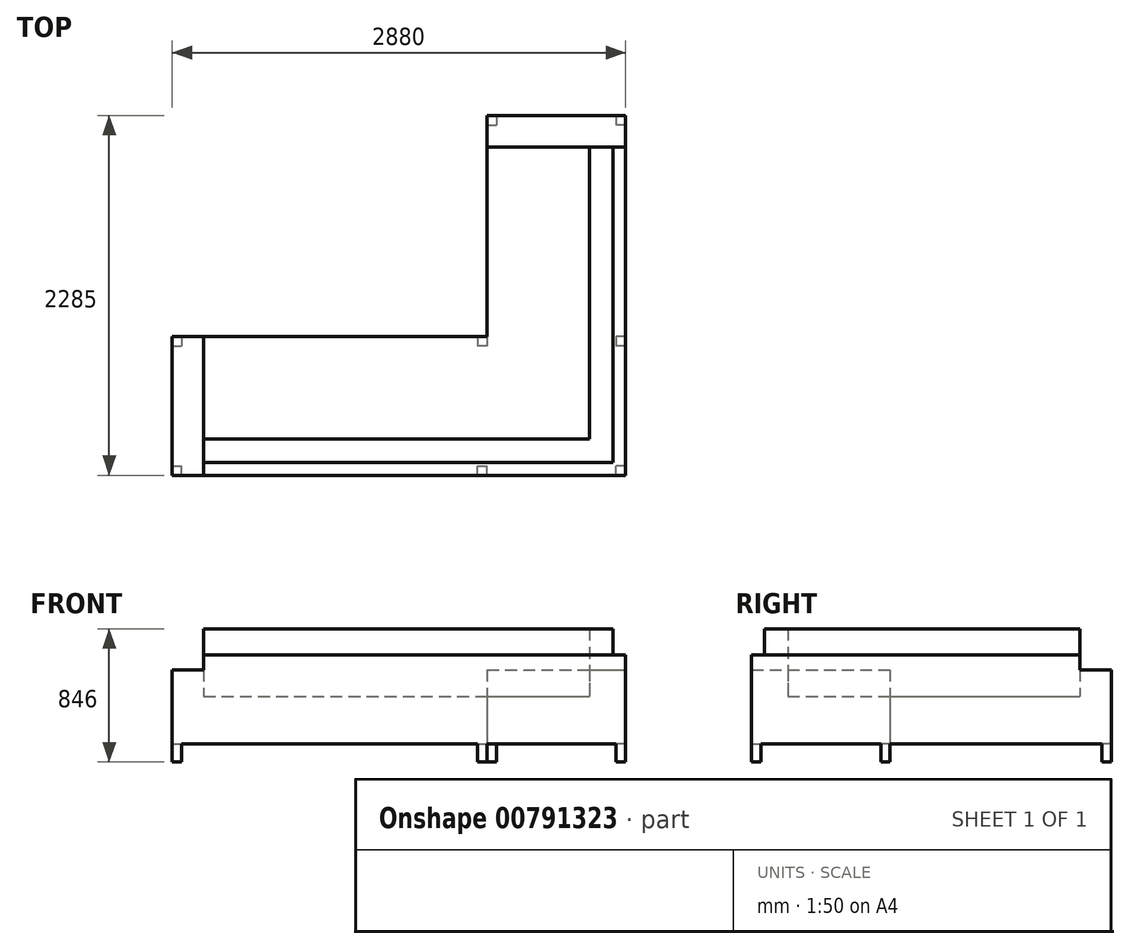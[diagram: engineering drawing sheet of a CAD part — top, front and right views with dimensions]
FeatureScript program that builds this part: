
annotation { "Feature Type Name" : "Feature", "Feature Type Description" : "" }
export const myFeature = defineFeature(function(context is Context, id is Id, definition is map)
    precondition{}
    {
        {
            var Q0;
            Q0=qCreatedBy(makeId("Top.planeOp"),FACE);
            var sketch = newSketch(context, id + "F0", { "sketchPlane" : qUnion([Q0])});
            skLineSegment(sketch, "E0", {"start": v(0, 0) * mm, "end": v(0, 1405) * mm});
            skLineSegment(sketch, "E1", {"start": v(0, 1405) * mm, "end": v(880, 1405) * mm});
            skLineSegment(sketch, "E2", {"start": v(880, 1405) * mm, "end": v(880, -880) * mm});
            skLineSegment(sketch, "E3", {"start": v(880, -880) * mm, "end": v(-2000, -880) * mm});
            skLineSegment(sketch, "E4", {"start": v(-2000, -880) * mm, "end": v(-2000, 0) * mm});
            skLineSegment(sketch, "E5", {"start": v(-2000, 0) * mm, "end": v(0, 0) * mm});
            skSolve(sketch);
        }
        {
            var Q0;
            Q0=makeQuery(id+"F0.imprint","IMPRINT",FACE,{"disambiguationData":[TD([[makeQuery(id+"F0.imprint","IMPRINT",EDGE,{"derivedFrom":sQuery(id+"F0.wireOp",EDGE,"E0")}),-1.0]])]});
            extrude(context, id + "F1", {"entities" : qUnion([Q0]), "depth" : 300 * mm, "offsetDistance" : 25 * mm});
        }
        {
            var Q0;
            Q0=makeQuery(id+"F1.opExtrude","CAP_FACE",FACE,{"disambiguationData":[OSD([sQuery(id+"F0.wireOp",EDGE,"E0"),sQuery(id+"F0.wireOp",EDGE,"E1"),sQuery(id+"F0.wireOp",EDGE,"E2"),sQuery(id+"F0.wireOp",EDGE,"E3"),sQuery(id+"F0.wireOp",EDGE,"E4"),sQuery(id+"F0.wireOp",EDGE,"E5")])],"isStart":true});
            var sketch = newSketch(context, id + "F2", { "sketchPlane" : qUnion([Q0])});
            skLineSegment(sketch, "E6.bottom", {"start": v(0, -1405) * mm, "end": v(60, -1405) * mm});
            skLineSegment(sketch, "E6.top", {"start": v(0, -1345) * mm, "end": v(60, -1345) * mm});
            skLineSegment(sketch, "E6.left", {"start": v(0, -1405) * mm, "end": v(0, -1345) * mm});
            skLineSegment(sketch, "E6.right", {"start": v(60, -1405) * mm, "end": v(60, -1345) * mm});
            skLineSegment(sketch, "E7.bottom", {"start": v(880, -1405) * mm, "end": v(820, -1405) * mm});
            skLineSegment(sketch, "E7.top", {"start": v(880, -1345) * mm, "end": v(820, -1345) * mm});
            skLineSegment(sketch, "E7.left", {"start": v(880, -1405) * mm, "end": v(880, -1345) * mm});
            skLineSegment(sketch, "E7.right", {"start": v(820, -1405) * mm, "end": v(820, -1345) * mm});
            skLineSegment(sketch, "E8.bottom", {"start": v(-2000, 0) * mm, "end": v(-1940, 0) * mm});
            skLineSegment(sketch, "E8.top", {"start": v(-2000, 60) * mm, "end": v(-1940, 60) * mm});
            skLineSegment(sketch, "E8.left", {"start": v(-2000, 0) * mm, "end": v(-2000, 60) * mm});
            skLineSegment(sketch, "E8.right", {"start": v(-1940, 0) * mm, "end": v(-1940, 60) * mm});
            skLineSegment(sketch, "E9.bottom", {"start": v(-2000, 880) * mm, "end": v(-1940, 880) * mm});
            skLineSegment(sketch, "E9.top", {"start": v(-2000, 820) * mm, "end": v(-1940, 820) * mm});
            skLineSegment(sketch, "E9.left", {"start": v(-2000, 880) * mm, "end": v(-2000, 820) * mm});
            skLineSegment(sketch, "E9.right", {"start": v(-1940, 880) * mm, "end": v(-1940, 820) * mm});
            skLineSegment(sketch, "E10.bottom", {"start": v(0, 0) * mm, "end": v(-60, 0) * mm});
            skLineSegment(sketch, "E10.top", {"start": v(0, 60) * mm, "end": v(-60, 60) * mm});
            skLineSegment(sketch, "E10.left", {"start": v(0, 0) * mm, "end": v(0, 60) * mm});
            skLineSegment(sketch, "E10.right", {"start": v(-60, 0) * mm, "end": v(-60, 60) * mm});
            skLineSegment(sketch, "E11.bottom", {"start": v(-60, 880) * mm, "end": v(0, 880) * mm});
            skLineSegment(sketch, "E11.top", {"start": v(-60, 820) * mm, "end": v(0, 820) * mm});
            skLineSegment(sketch, "E11.left", {"start": v(-60, 880) * mm, "end": v(-60, 820) * mm});
            skLineSegment(sketch, "E11.right", {"start": v(0, 880) * mm, "end": v(0, 820) * mm});
            skLineSegment(sketch, "E12.bottom", {"start": v(880, 880) * mm, "end": v(820, 880) * mm});
            skLineSegment(sketch, "E12.top", {"start": v(880, 820) * mm, "end": v(820, 820) * mm});
            skLineSegment(sketch, "E12.left", {"start": v(880, 880) * mm, "end": v(880, 820) * mm});
            skLineSegment(sketch, "E12.right", {"start": v(820, 880) * mm, "end": v(820, 820) * mm});
            skLineSegment(sketch, "E13.bottom", {"start": v(880, 0) * mm, "end": v(820, 0) * mm});
            skLineSegment(sketch, "E13.top", {"start": v(880, 60) * mm, "end": v(820, 60) * mm});
            skLineSegment(sketch, "E13.left", {"start": v(880, 0) * mm, "end": v(880, 60) * mm});
            skLineSegment(sketch, "E13.right", {"start": v(820, 0) * mm, "end": v(820, 60) * mm});
            skSolve(sketch);
        }
        {
            var Q0;
            Q0=makeQuery(id+"F2.imprint","IMPRINT",FACE,{"disambiguationData":[TD([[makeQuery(id+"F2.imprint","IMPRINT",EDGE,{"derivedFrom":sQuery(id+"F2.wireOp",EDGE,"E9.bottom")}),1.0]])]});
            var Q1;
            Q1=makeQuery(id+"F2.imprint","IMPRINT",FACE,{"disambiguationData":[TD([[makeQuery(id+"F2.imprint","IMPRINT",EDGE,{"derivedFrom":sQuery(id+"F2.wireOp",EDGE,"E8.bottom")}),1.0]])]});
            var Q2;
            Q2=makeQuery(id+"F2.imprint","IMPRINT",FACE,{"disambiguationData":[TD([[makeQuery(id+"F2.imprint","IMPRINT",EDGE,{"derivedFrom":sQuery(id+"F2.wireOp",EDGE,"E10.bottom")}),1.0]])]});
            var Q3;
            Q3=makeQuery(id+"F2.imprint","IMPRINT",FACE,{"disambiguationData":[TD([[makeQuery(id+"F2.imprint","IMPRINT",EDGE,{"derivedFrom":sQuery(id+"F2.wireOp",EDGE,"E11.bottom")}),1.0]])]});
            var Q4;
            Q4=makeQuery(id+"F2.imprint","IMPRINT",FACE,{"disambiguationData":[TD([[makeQuery(id+"F2.imprint","IMPRINT",EDGE,{"derivedFrom":sQuery(id+"F2.wireOp",EDGE,"E12.bottom")}),1.0]])]});
            var Q5;
            Q5=makeQuery(id+"F2.imprint","IMPRINT",FACE,{"disambiguationData":[TD([[makeQuery(id+"F2.imprint","IMPRINT",EDGE,{"derivedFrom":sQuery(id+"F2.wireOp",EDGE,"E13.bottom")}),-1.0]])]});
            var Q6;
            Q6=makeQuery(id+"F2.imprint","IMPRINT",FACE,{"disambiguationData":[TD([[makeQuery(id+"F2.imprint","IMPRINT",EDGE,{"derivedFrom":sQuery(id+"F2.wireOp",EDGE,"E6.bottom")}),1.0]])]});
            var Q7;
            Q7=makeQuery(id+"F2.imprint","IMPRINT",FACE,{"disambiguationData":[TD([[makeQuery(id+"F2.imprint","IMPRINT",EDGE,{"derivedFrom":sQuery(id+"F2.wireOp",EDGE,"E7.bottom")}),1.0]])]});
            extrude(context, id + "F3", {"entities" : qUnion([Q0, Q1, Q2, Q3, Q4, Q5, Q6, Q7]), "operationType" : NewBodyOperationType.ADD, "depth" : 116 * mm, "offsetDistance" : 25 * mm});
        }
        {
            var Q0;
            Q0=makeQuery(id+"F1.opExtrude","CAP_FACE",FACE,{"disambiguationData":[OSD([sQuery(id+"F0.wireOp",EDGE,"E0"),sQuery(id+"F0.wireOp",EDGE,"E1"),sQuery(id+"F0.wireOp",EDGE,"E2"),sQuery(id+"F0.wireOp",EDGE,"E3"),sQuery(id+"F0.wireOp",EDGE,"E4"),sQuery(id+"F0.wireOp",EDGE,"E5")])],"isStart":false});
            var sketch = newSketch(context, id + "F4", { "sketchPlane" : qUnion([Q0])});
            skLineSegment(sketch, "E14.bottom", {"start": v(0, 1405) * mm, "end": v(880, 1405) * mm});
            skLineSegment(sketch, "E14.top", {"start": v(0, 1205) * mm, "end": v(880, 1205) * mm});
            skLineSegment(sketch, "E14.left", {"start": v(0, 1405) * mm, "end": v(0, 1205) * mm});
            skLineSegment(sketch, "E14.right", {"start": v(880, 1405) * mm, "end": v(880, 1205) * mm});
            skLineSegment(sketch, "E15.bottom", {"start": v(-2000, -880) * mm, "end": v(-1800, -880) * mm});
            skLineSegment(sketch, "E15.top", {"start": v(-2000, 0) * mm, "end": v(-1800, 0) * mm});
            skLineSegment(sketch, "E15.left", {"start": v(-2000, -880) * mm, "end": v(-2000, 0) * mm});
            skLineSegment(sketch, "E15.right", {"start": v(-1800, -880) * mm, "end": v(-1800, 0) * mm});
            skSolve(sketch);
        }
        {
            var Q0;
            Q0=makeQuery(id+"F4.imprint","IMPRINT",FACE,{"disambiguationData":[TD([[makeQuery(id+"F4.imprint","IMPRINT",EDGE,{"derivedFrom":sQuery(id+"F4.wireOp",EDGE,"E14.bottom")}),-1.0]])]});
            var Q1;
            Q1=makeQuery(id+"F4.imprint","IMPRINT",FACE,{"disambiguationData":[TD([[makeQuery(id+"F4.imprint","IMPRINT",EDGE,{"derivedFrom":sQuery(id+"F4.wireOp",EDGE,"E15.bottom")}),-1.0]])]});
            extrude(context, id + "F5", {"entities" : qUnion([Q0, Q1]), "operationType" : NewBodyOperationType.ADD, "depth" : 170 * mm, "offsetDistance" : 25 * mm});
        }
        {
            var Q0;
            Q0=makeQuery(id+"F1.opExtrude","CAP_FACE",FACE,{"disambiguationData":[OSD([sQuery(id+"F0.wireOp",EDGE,"E0"),sQuery(id+"F0.wireOp",EDGE,"E1"),sQuery(id+"F0.wireOp",EDGE,"E2"),sQuery(id+"F0.wireOp",EDGE,"E3"),sQuery(id+"F0.wireOp",EDGE,"E4"),sQuery(id+"F0.wireOp",EDGE,"E5")])],"isStart":false});
            var sketch = newSketch(context, id + "F6", { "sketchPlane" : qUnion([Q0])});
            skLineSegment(sketch, "E16.bottom", {"start": v(880, 1205) * mm, "end": v(800, 1205) * mm});
            skLineSegment(sketch, "E16.top", {"start": v(880, -880) * mm, "end": v(800, -880) * mm});
            skLineSegment(sketch, "E16.left", {"start": v(880, 1205) * mm, "end": v(880, -880) * mm});
            skLineSegment(sketch, "E16.right", {"start": v(800, 1205) * mm, "end": v(800, -800) * mm});
            skLineSegment(sketch, "E17.bottom", {"start": v(800, -880) * mm, "end": v(-1800, -880) * mm});
            skLineSegment(sketch, "E17.top", {"start": v(800, -800) * mm, "end": v(-1800, -800) * mm});
            skLineSegment(sketch, "E17.right", {"start": v(-1800, -880) * mm, "end": v(-1800, -800) * mm});
            skSolve(sketch);
        }
        {
            var Q0;
            Q0=makeQuery(id+"F6.imprint","IMPRINT",FACE,{"disambiguationData":[TD([[makeQuery(id+"F6.imprint","IMPRINT",EDGE,{"derivedFrom":sQuery(id+"F6.wireOp",EDGE,"E16.bottom")}),-1.0]])]});
            extrude(context, id + "F7", {"entities" : qUnion([Q0]), "operationType" : NewBodyOperationType.ADD, "depth" : 265 * mm, "offsetDistance" : 25 * mm});
        }
        {
            var Q0;
            Q0=makeQuery(id+"F1.opExtrude","CAP_FACE",FACE,{"disambiguationData":[OSD([sQuery(id+"F0.wireOp",EDGE,"E0"),sQuery(id+"F0.wireOp",EDGE,"E1"),sQuery(id+"F0.wireOp",EDGE,"E2"),sQuery(id+"F0.wireOp",EDGE,"E3"),sQuery(id+"F0.wireOp",EDGE,"E4"),sQuery(id+"F0.wireOp",EDGE,"E5")])],"isStart":false});
            var sketch = newSketch(context, id + "F8", { "sketchPlane" : qUnion([Q0])});
            skLineSegment(sketch, "E18.bottom", {"start": v(800, -800) * mm, "end": v(650, -800) * mm});
            skLineSegment(sketch, "E18.top", {"start": v(800, 1205) * mm, "end": v(650, 1205) * mm});
            skLineSegment(sketch, "E18.left", {"start": v(800, -800) * mm, "end": v(800, 1205) * mm});
            skLineSegment(sketch, "E18.right", {"start": v(650, -650) * mm, "end": v(650, 1205) * mm});
            skLineSegment(sketch, "E19.bottom", {"start": v(-1800, -800) * mm, "end": v(650, -800) * mm});
            skLineSegment(sketch, "E19.top", {"start": v(-1800, -650) * mm, "end": v(650, -650) * mm});
            skLineSegment(sketch, "E19.left", {"start": v(-1800, -800) * mm, "end": v(-1800, -650) * mm});
            skSolve(sketch);
        }
        {
            var Q0;
            Q0=makeQuery(id+"F8.imprint","IMPRINT",FACE,{"disambiguationData":[TD([[makeQuery(id+"F8.imprint","IMPRINT",EDGE,{"derivedFrom":sQuery(id+"F8.wireOp",EDGE,"E18.bottom")}),-1.0]])]});
            extrude(context, id + "F9", {"entities" : qUnion([Q0]), "operationType" : NewBodyOperationType.ADD, "depth" : 430 * mm, "offsetDistance" : 25 * mm});
        }
    });
